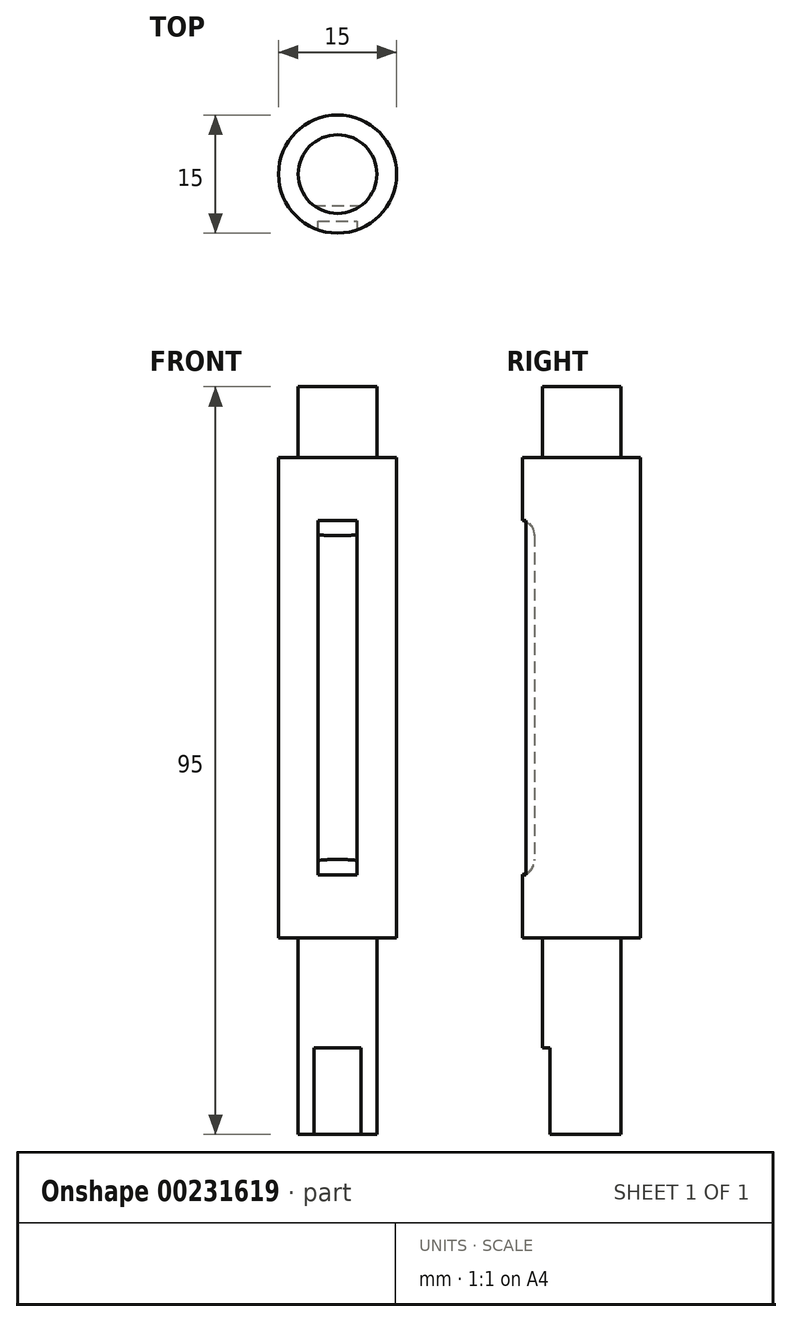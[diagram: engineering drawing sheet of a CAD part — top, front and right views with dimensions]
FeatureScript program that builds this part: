
annotation { "Feature Type Name" : "Feature", "Feature Type Description" : "" }
export const myFeature = defineFeature(function(context is Context, id is Id, definition is map)
    precondition{}
    {
        {
            var Q0;
            Q0=qCreatedBy(makeId("Top.planeOp"),FACE);
            var sketch = newSketch(context, id + "F0", { "sketchPlane" : qUnion([Q0])});
            skCircle(sketch, "E0", {"center": v(0, 0) * mm, "radius": 7.5 * mm});
            skSolve(sketch);
        }
        {
            var Q0;
            Q0=makeQuery(id+"F0.imprint","IMPRINT",FACE,{"disambiguationData":[TD([[makeQuery(id+"F0.imprint","IMPRINT",EDGE,{"derivedFrom":sQuery(id+"F0.wireOp",EDGE,"E0")}),1.0]])]});
            extrude(context, id + "F1", {"entities" : qUnion([Q0]), "depth" : 61 * mm});
        }
        {
            var Q0;
            Q0=makeQuery(id+"F1.opExtrude","CAP_FACE",FACE,{"disambiguationData":[OSD([sQuery(id+"F0.wireOp",EDGE,"E0")])],"isStart":true});
            var sketch = newSketch(context, id + "F2", { "sketchPlane" : qUnion([Q0])});
            skCircle(sketch, "E1", {"center": v(0, 0) * mm, "radius": 5 * mm});
            skSolve(sketch);
        }
        {
            var Q0;
            Q0 = qSketchRegion(id + "F2", true);
            extrude(context, id + "F3", {"entities" : qUnion([Q0]), "operationType" : NewBodyOperationType.ADD, "depth" : 25 * mm});
        }
        {
            var Q0;
            Q0=makeQuery(id+"F3.opExtrude","CAP_FACE",FACE,{"disambiguationData":[OSD([sQuery(id+"F2.wireOp",EDGE,"E1")])],"isStart":false});
            var sketch = newSketch(context, id + "F4", { "sketchPlane" : qUnion([Q0])});
            skLineSegment(sketch, "E2.bottom", {"start": v(-5.75, 8.44) * mm, "end": v(7.04, 8.44) * mm});
            skLineSegment(sketch, "E2.top", {"start": v(-5.75, 4) * mm, "end": v(7.04, 4) * mm});
            skLineSegment(sketch, "E2.left", {"start": v(-5.75, 8.44) * mm, "end": v(-5.75, 4) * mm});
            skLineSegment(sketch, "E2.right", {"start": v(7.04, 8.44) * mm, "end": v(7.04, 4) * mm});
            skSolve(sketch);
        }
        {
            var Q0;
            Q0 = qSketchRegion(id + "F4", true);
            extrude(context, id + "F5", {"entities" : qUnion([Q0]), "operationType" : NewBodyOperationType.REMOVE, "oppositeDirection" : true, "depth" : (25 - 14) * mm});
        }
        {
            var Q0;
            Q0=makeQuery(id+"F1.opExtrude","CAP_FACE",FACE,{"disambiguationData":[OSD([sQuery(id+"F0.wireOp",EDGE,"E0")])],"isStart":false});
            var sketch = newSketch(context, id + "F6", { "sketchPlane" : qUnion([Q0])});
            skCircle(sketch, "E3", {"center": v(0, 0) * mm, "radius": 5 * mm});
            skSolve(sketch);
        }
        {
            var Q0;
            Q0 = qSketchRegion(id + "F6", true);
            extrude(context, id + "F7", {"entities" : qUnion([Q0]), "operationType" : NewBodyOperationType.ADD, "depth" : 9 * mm});
        }
        {
            var Q0;
            Q0=qCreatedBy(makeId("Front.planeOp"),FACE);
            var sketch = newSketch(context, id + "F8", { "sketchPlane" : qUnion([Q0])});
            skLineSegment(sketch, "E4.bottom", {"start": v(-2.5, 53) * mm, "end": v(2.5, 53) * mm});
            skLineSegment(sketch, "E4.top", {"start": v(-2.5, 8) * mm, "end": v(2.5, 8) * mm});
            skLineSegment(sketch, "E4.left", {"start": v(-2.5, 53) * mm, "end": v(-2.5, 8) * mm});
            skLineSegment(sketch, "E4.right", {"start": v(2.5, 53) * mm, "end": v(2.5, 8) * mm});
            skPoint(sketch, "E5", {"position": v(2.5, 30.5) * mm});
            skPoint(sketch, "E6", {"position": v(12.13, 61) * mm});
            skPoint(sketch, "E7", {"position": v(0, 53) * mm});
            skSolve(sketch);
        }
        {
            var Q0;
            Q0 = qSketchRegion(id + "F8", true);
            extrude(context, id + "F9", {"entities" : qUnion([Q0]), "operationType" : NewBodyOperationType.REMOVE, "depth" : 25 * mm, "hasSecondDirection" : true, "secondDirectionOppositeDirection" : false, "secondDirectionDepth" : 6 * mm});
        }
        {
            var Q0;
            Q0=makeQuery(id+"F9.boolean.opBoolean","COPY",EDGE,{"derivedFrom":makeQuery(id+"F9.opExtrude","CAP_EDGE",EDGE,{"disambiguationData":[OSD([sQuery(id+"F8.wireOp",EDGE,"E4.bottom")])],"isStart":true})});
            var Q1;
            Q1=makeQuery(id+"F9.boolean.opBoolean","COPY",EDGE,{"derivedFrom":makeQuery(id+"F9.opExtrude","CAP_EDGE",EDGE,{"disambiguationData":[OSD([sQuery(id+"F8.wireOp",EDGE,"E4.top")])],"isStart":true})});
            fillet(context, id + "F10", {"entities" : qUnion([Q0, Q1]), "radius" : 2 * mm, "tangentPropagation" : true, "allowEdgeOverflow" : false});
        }
    });
